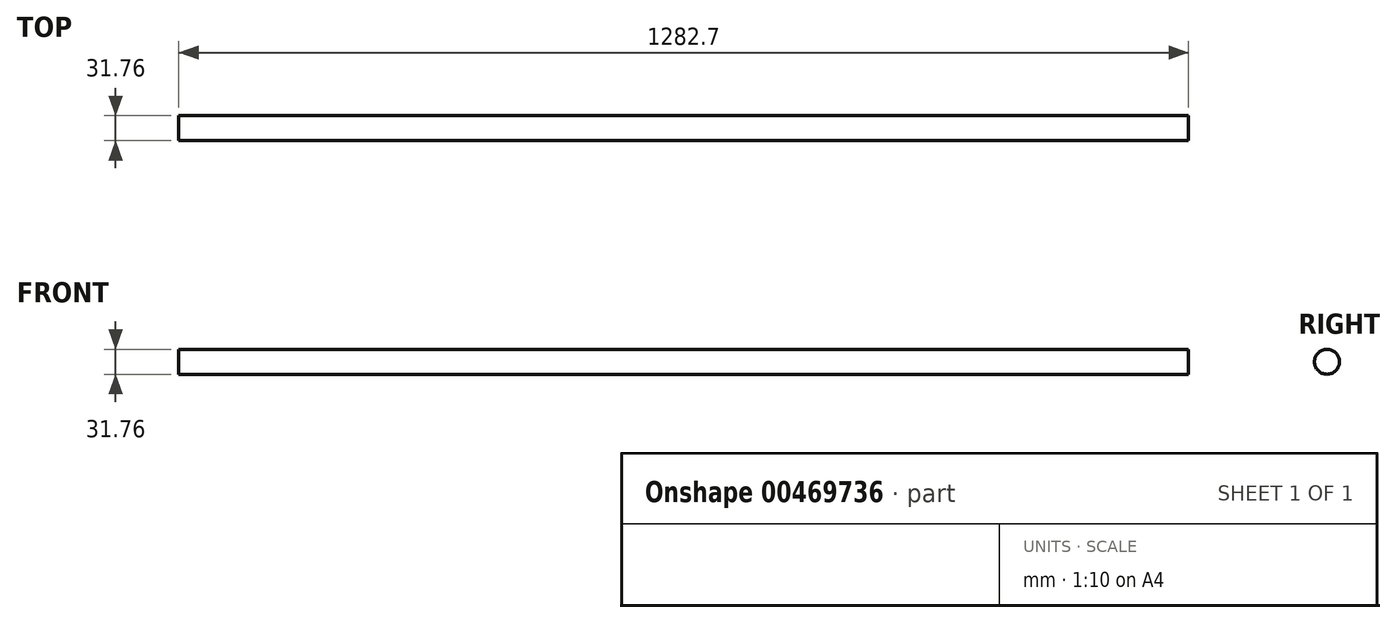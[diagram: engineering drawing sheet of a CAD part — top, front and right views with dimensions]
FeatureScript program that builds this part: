
annotation { "Feature Type Name" : "Feature", "Feature Type Description" : "" }
export const myFeature = defineFeature(function(context is Context, id is Id, definition is map)
    precondition{}
    {
        {
            var Q0;
            Q0=qCreatedBy(makeId("Right.planeOp"),FACE);
            var sketch = newSketch(context, id + "F0", { "sketchPlane" : qUnion([Q0])});
            skCircle(sketch, "E0", {"center": v(0, 0) * mm, "radius": 15.88 * mm});
            skSolve(sketch);
        }
        {
            var Q0;
            Q0=makeQuery(id+"F0.imprint","IMPRINT",FACE,{"disambiguationData":[TD([[makeQuery(id+"F0.imprint","IMPRINT",EDGE,{"derivedFrom":sQuery(id+"F0.wireOp",EDGE,"E0")}),1.0]])]});
            extrude(context, id + "F1", {"entities" : qUnion([Q0]), "depth" : 1282.7 * mm, "offsetDistance" : 25.4 * mm});
        }
    });
